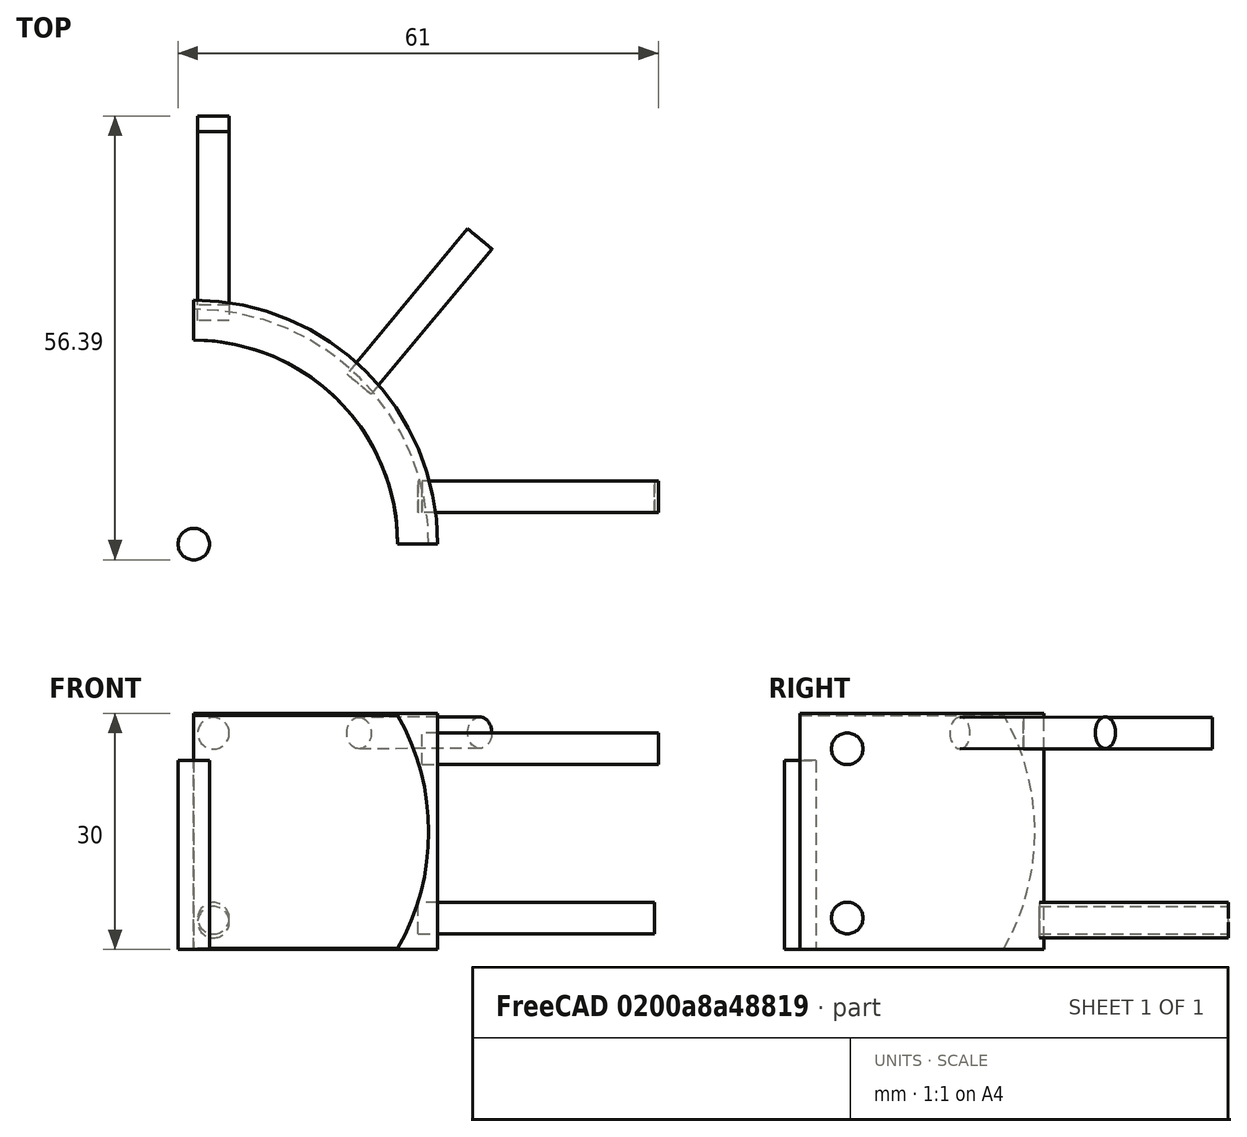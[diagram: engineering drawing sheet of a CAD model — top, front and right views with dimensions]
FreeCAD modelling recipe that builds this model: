
FCSTD DOCUMENT  (FreeCAD 1.1R43946 (Git))
Label: door_handle-slice
License: All rights reserved
LicenseURL: https://en.wikipedia.org/wiki/All_rights_reserved
objects: Part::Cylinder×7, Sketcher::SketchObject×3, Mesh::Feature×3, App::Point×2, PartDesign::FeatureBase×1, PartDesign::Pad×1, PartDesign::Groove×1, PartDesign::Body×1, App::Part×1
note: 22 computed .brp shape members not serialized (recipe doc carries the construction recipe); baked Part::Feature solids carry a one-line shape summary decoded from their .brp

FEATURE [Sketcher::SketchObject] Sketch
  ArcFitTolerance = 1e-06
  AttachmentSupport = -> [Origin]
  ExternalTypes = [0]
  FullyConstrained = true
  MakeInternals = false
  MapMode = 5
  sketch-geometry (6):
    g0: ArcOfCircle CenterX=0 CenterY=0 CenterZ=0 NormalX=0 NormalY=0 NormalZ=1 AngleXU=0 Radius=25.9 StartAngle=3.26795e-07 EndAngle=1.5708
    g1: LineSegment StartX=1.6e-15 StartY=25.9 StartZ=0 EndX=1.6e-15 EndY=30.9 EndZ=0
    g2: LineSegment StartX=25.9 StartY=8.46399e-06 StartZ=0 EndX=30.9 EndY=0 EndZ=0
    g3: ArcOfCircle CenterX=0 CenterY=0 CenterZ=0 NormalX=0 NormalY=0 NormalZ=1 AngleXU=0 Radius=30.98 StartAngle=0 EndAngle=1.5708
    g4: LineSegment StartX=30.9 StartY=0 StartZ=0 EndX=30.98 EndY=0 EndZ=0
    g5: LineSegment StartX=1.6e-15 StartY=30.9 StartZ=0 EndX=1.9e-15 EndY=30.98 EndZ=0
  constraints (18):
    c: Radius(g0) = 25.9
    c: Angle(g0) = 1.5708
    c: Coincident(g0,g-1)
    c: Distance(g1) = 5
    c: Coincident(g1,g0)
    c: PointOnObject(g1,g-2)
    c: Vertical(g1)
    c: Distance(g2) = 5
    c: Coincident(g2,g0)
    c: PointOnObject(g2,g-1)
    c: Radius(g3) = 30.98
    c: Coincident(g3,g0)
    c: PointOnObject(g3,g-2)
    c: PointOnObject(g3,g-1)
    c: Coincident(g4,g2)
    c: Coincident(g4,g3)
    c: Coincident(g5,g1)
    c: Coincident(g5,g3)
FEATURE [App::Point] Origin001
  Role = Origin
FEATURE [Sketcher::SketchObject] Sketch001
  ArcFitTolerance = 1e-06
  AttachmentSupport = -> [Origin]
  ExternalTypes = [0]
  FullyConstrained = false
  MakeInternals = false
  MapMode = 5
  Placement = pos=(0,0,0) rot=(1,0,0;1.5708rad)
  sketch-geometry (2):
    g0: ArcOfCircle CenterX=0 CenterY=14.9449 CenterZ=0 NormalX=0 NormalY=0 NormalZ=1 AngleXU=0 Radius=29.841 StartAngle=5.75864 EndAngle=6.80773
    g1: LineSegment StartX=25.8289 StartY=29.8898 StartZ=0 EndX=25.8289 EndY=-1.07e-14 EndZ=0
  constraints (5):
    c: PointOnObject(g0,g-2)
    c: PointOnObject(g0,g-1)
    c: Coincident(g1,g0)
    c: Coincident(g1,g0)
    c: Parallel(g1,g-2)
FEATURE [App::Point] Origin003
  Role = Origin
FEATURE [Mesh::Feature] doornob_arc
  Placement = pos=(191,148,0) rot=(0,0,1;3.14159rad)
FEATURE [Part::Cylinder] Cylinder006
  Angle = 360
  AttacherType = Attacher::AttachEngine3D
  FirstAngle = 0
  Height = 24
  Placement = pos=(2.5,52.39,27.47) rot=(1,0,0;1.5708rad)
  Radius = 2
  SecondAngle = 0
FEATURE [Part::Cylinder] Cylinder007
  Angle = 360
  AttacherType = Attacher::AttachEngine3D
  FirstAngle = 0
  Height = 24
  Placement = pos=(2.5,54.39,3.97) rot=(1,0,0;1.5708rad)
  Radius = 2
  SecondAngle = 0
FEATURE [Part::Cylinder] Cylinder
  Angle = 360
  AttacherType = Attacher::AttachEngine3D
  FirstAngle = 0
  Height = 30
  Placement = pos=(29,6,25.5) rot=(0,1,0;1.5708rad)
  Radius = 2
  SecondAngle = 0
FEATURE [Part::Cylinder] Cylinder008
  Angle = 360
  AttacherType = Attacher::AttachEngine3D
  FirstAngle = 0
  Height = 24
  Placement = pos=(2.5,54.39,3.47) rot=(1,0,0;1.5708rad)
  Radius = 2
  SecondAngle = 0
FEATURE [Part::Cylinder] Cylinder009
  Angle = 360
  AttacherType = Attacher::AttachEngine3D
  FirstAngle = 0
  Height = 24
  Placement = pos=(20.9857,20.3292,27.4999) rot=(0.39,-0.83,-0.39;4.5328rad)
  Radius = 2
  SecondAngle = 0
FEATURE [Part::Cylinder] Cylinder010
  Angle = 360
  AttacherType = Attacher::AttachEngine3D
  FirstAngle = 0
  Height = 30
  Placement = pos=(28.5,6,4) rot=(0,1,0;1.5708rad)
  Radius = 2
  SecondAngle = 0
FEATURE [Part::Cylinder] Cylinder011
  Angle = 360
  AttacherType = Attacher::AttachEngine3D
  FirstAngle = 0
  Height = 24
  Placement = pos=(21.03,20.35,4) rot=(0.39,-0.83,-0.39;4.5328rad)
  Radius = 2
  SecondAngle = 0
FEATURE [PartDesign::FeatureBase] BaseFeature
  BaseFeature = -> Cylinder011
  Suppressed = false
FEATURE [PartDesign::Pad] Pad
  BaseFeature = -> BaseFeature
  Direction = (0,0,1)
  Length = 30
  Length2 = 10
  Profile = -> Sketch
  ReferenceAxis = -> Sketch [N_Axis]
  Refine = true
  SideType = 0
  Suppressed = false
  Type = 0
  Type2 = 0
FEATURE [Sketcher::SketchObject] Sketch002
  ArcFitTolerance = 1e-06
  AttachmentSupport = -> [Pad]
  ExternalTypes = [0]
  FullyConstrained = true
  MakeInternals = false
  MapMode = 5
  Placement = pos=(1.9e-15,0,0) rot=(0.57735,-0.57735,-0.57735;2.0944rad)
FEATURE [PartDesign::Groove] Groove
  Angle = 360
  Angle2 = 0
  Axis = (0,2e-16,1)
  Base = (0,0,0)
  BaseFeature = -> Pad
  Profile = -> Sketch001
  ReferenceAxis = -> Sketch001 [V_Axis]
  Refine = true
  Suppressed = false
  Type = 0
FEATURE [PartDesign::Body] Body
  AllowCompound = true
  BaseFeature = -> Cylinder011
  Group = -> [BaseFeature,Sketch,Pad,Sketch001,Groove]
  Origin = -> Origin
  Tip = -> Groove
FEATURE [App::Part] Part
  Group = -> [Body,Cylinder010,Cylinder006,Cylinder007,Cylinder,Cylinder011,Cylinder008,Cylinder009]
  Origin = -> Origin002
FEATURE [Mesh::Feature] Mesh  label="Part (Meshed)"
FEATURE [Mesh::Feature] Mesh001
